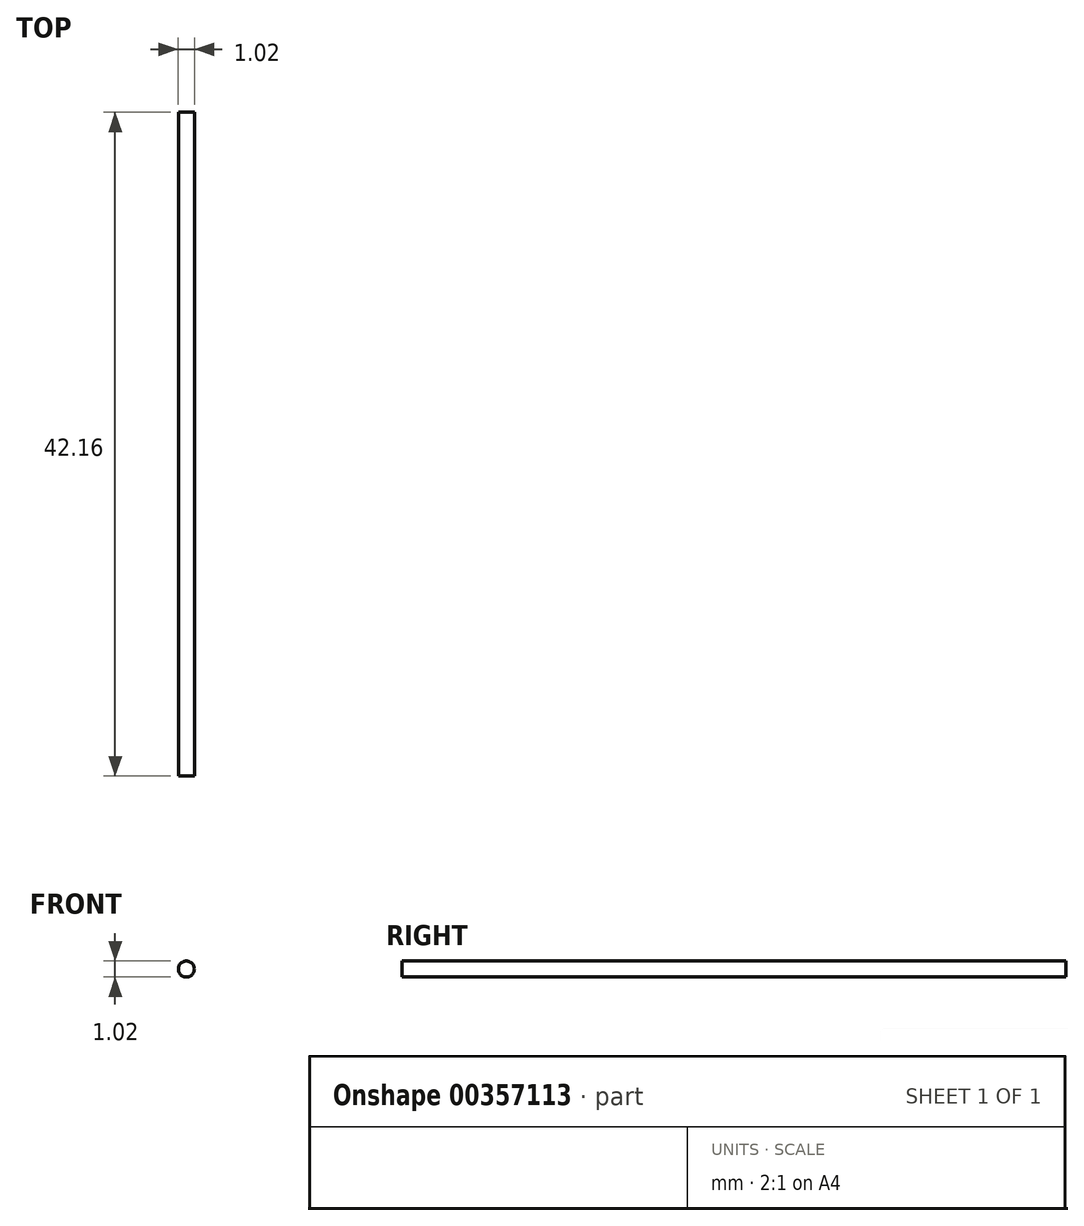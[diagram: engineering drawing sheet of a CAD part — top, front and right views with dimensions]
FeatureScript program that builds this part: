
annotation { "Feature Type Name" : "Feature", "Feature Type Description" : "" }
export const myFeature = defineFeature(function(context is Context, id is Id, definition is map)
    precondition{}
    {
        {
            var Q0;
            Q0=qCreatedBy(makeId("Front.planeOp"),FACE);
            var sketch = newSketch(context, id + "F0", { "sketchPlane" : qUnion([Q0])});
            skCircle(sketch, "E0", {"center": v(0, 0) * mm, "radius": 0.5 * mm});
            skSolve(sketch);
        }
        {
            var Q0;
            Q0 = qSketchRegion(id + "F0", true);
            extrude(context, id + "F1", {"entities" : qUnion([Q0]), "endBound" : BoundingType.SYMMETRIC, "depth" : 42.16 * mm});
        }
    });
